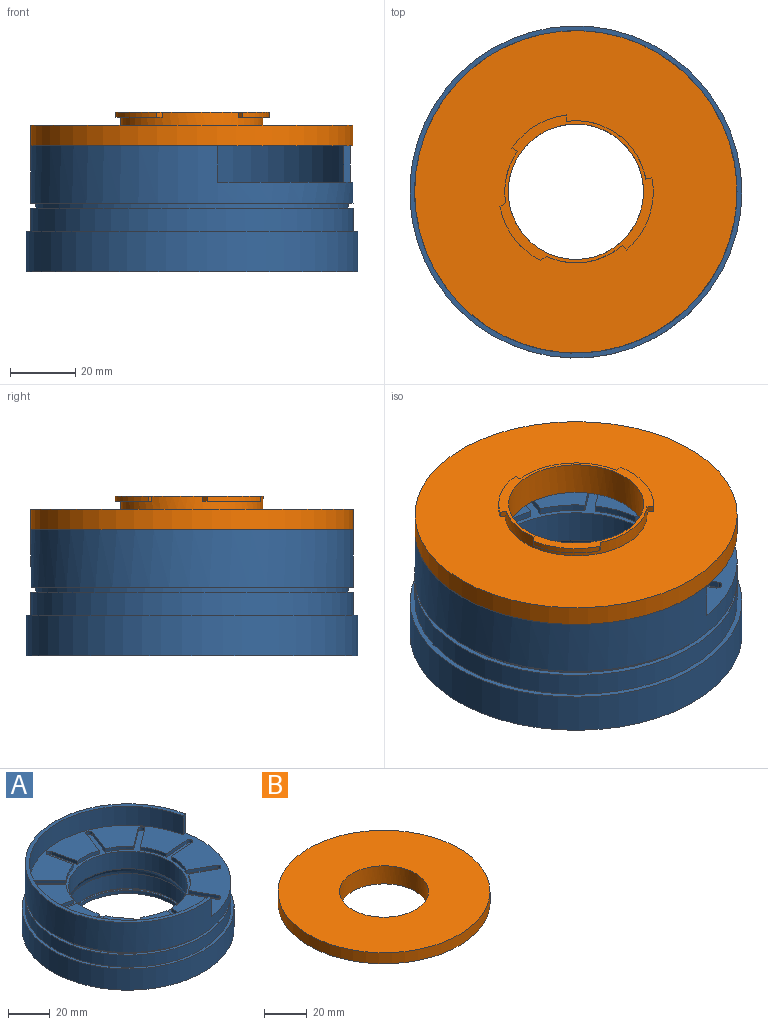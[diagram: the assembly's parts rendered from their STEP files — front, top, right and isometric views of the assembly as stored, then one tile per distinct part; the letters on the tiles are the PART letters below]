
ASSEMBLY  parts=2 mates=1
PART A: 65 faces, bbox 102.1x102.1x38.8 mm
  f0: cylinder r=49.57mm len=99.14mm, axis (0,0,-1), area 4618.4mm2, adj f2,f14,f22,f63,f64
  f1: cylinder r=47.57mm len=95.14mm, axis (0,0,-1), area 2494.3mm2, adj f2,f14,f63,f64
  f2: plane 97.14x96.49mm, normal (0,0,1), area 3856.3mm2, adj f0,f1,f3,f4,f5,f6,f7,f8
  f3: cylinder r=30mm len=9.74mm, axis (0,0,-1), area 27.8mm2, adj f2,f15,f32,f60
  f4: cylinder r=30mm len=13.45mm, axis (0,0,-1), area 27.8mm2, adj f2,f15,f57,f62
  f5: cylinder r=30mm len=12.9mm, axis (0,0,-1), area 27.8mm2, adj f2,f15,f54,f59
  f6: cylinder r=30mm len=11.01mm, axis (0,0,-1), area 27.8mm2, adj f2,f15,f51,f56
  f7: cylinder r=30mm len=13.73mm, axis (0,0,-1), area 27.8mm2, adj f2,f15,f48,f53
  f8: cylinder r=30mm len=12.08mm, axis (0,0,-1), area 27.8mm2, adj f2,f15,f45,f50
  f9: cylinder r=30mm len=12.07mm, axis (0,0,-1), area 27.8mm2, adj f2,f15,f42,f47
  f10: cylinder r=30mm len=13.73mm, axis (0,0,-1), area 27.8mm2, adj f2,f15,f39,f44
  f11: cylinder r=30mm len=11.02mm, axis (0,0,-1), area 27.8mm2, adj f2,f15,f36,f41
  f12: cylinder r=30mm len=12.89mm, axis (0,0,-1), area 27.8mm2, adj f2,f15,f33,f38
  f13: cylinder r=30mm len=13.45mm, axis (0,0,-1), area 27.8mm2, adj f2,f15,f30,f35
  f14: plane 99.14x98.22mm, normal (0,0,1), area 454.8mm2, adj f0,f1,f63,f64
  f15: plane 92x92mm, normal (0,0,1), area 842.9mm2, adj f3,f4,f5,f6,f7,f8,f9,f10
  f16: plane 102.14x102.14mm, normal (0,0,-1), area 5445.5mm2, adj f17,f29
  f17: cylinder r=51.07mm len=102.14mm, axis (0,0,1), area 4011mm2, adj f16,f18
  f18: plane 102.14x102.14mm, normal (0,0,1), area 474.2mm2, adj f17,f19
  f19: cylinder r=49.57mm len=99.14mm, axis (0,0,1), area 2216.5mm2, adj f18,f20
  f20: plane 99.14x99.14mm, normal (0,0,1), area 460.1mm2, adj f19,f21
  f21: cylinder r=48.07mm len=96.14mm, axis (0,0,1), area 453mm2, adj f20,f22
  f22: plane 99.14x99.14mm, normal (0,0,-1), area 460.1mm2, adj f0,f21
  f23: cylinder r=28.57mm len=57.15mm, axis (0,0,1), area 1838.8mm2, adj f15,f24
  f24: revolved ~59.15x59.15mm, area 686.4mm2, adj f23,f25
  f25: cylinder r=29.57mm len=59.15mm, axis (0,0,1), area 1635.3mm2, adj f24,f26
  f26: plane 61.15x61.15mm, normal (0,0,-1), area 189mm2, adj f25,f27
  f27: cylinder r=30.58mm len=61.15mm, axis (0,0,1), area 192.1mm2, adj f26,f28
  f28: plane 61.15x61.15mm, normal (0,0,1), area 189mm2, adj f27,f29
  f29: cylinder r=29.57mm len=59.15mm, axis (0,0,1), area 371.7mm2, adj f16,f28
  f30: plane 13.14x7.18mm, normal (0.88,0.48,0), area 29.9mm2, adj f2,f13,f15,f31
  f31: cylinder r=1.64mm len=3.08mm, axis (0,0,1), area 9.7mm2, adj f2,f15,f30,f32
  f32: plane 13.42x7.33mm, normal (-0.88,-0.48,0), area 30.6mm2, adj f2,f3,f15,f31
  f33: plane 14.94x2mm, normal (1,-0.07,0), area 29.9mm2, adj f2,f12,f15,f34
  f34: cylinder r=1.64mm len=3.22mm, axis (0,0,1), area 9.7mm2, adj f2,f15,f33,f35
  f35: plane 15.25x2mm, normal (-1,0.07,0), area 30.6mm2, adj f2,f13,f15,f34
  f36: plane 11.99x8.97mm, normal (0.8,-0.6,0), area 29.9mm2, adj f2,f11,f15,f37
  f37: cylinder r=1.64mm len=2.74mm, axis (0,0,1), area 9.7mm2, adj f2,f15,f36,f38
  f38: plane 12.24x9.16mm, normal (-0.8,0.6,0), area 30.6mm2, adj f2,f12,f15,f37
  f39: plane 14.03x5.23mm, normal (0.35,-0.94,0), area 29.9mm2, adj f2,f10,f15,f40
  f40: cylinder r=1.64mm len=3.18mm, axis (0,0,1), area 9.7mm2, adj f2,f15,f39,f41
  f41: plane 14.32x5.34mm, normal (-0.35,0.94,0), area 30.6mm2, adj f2,f11,f15,f40
  f42: plane 14.63x3.18mm, normal (-0.21,-0.98,0), area 29.9mm2, adj f2,f9,f15,f43
  f43: cylinder r=1.64mm len=3.15mm, axis (0,0,1), area 9.7mm2, adj f2,f15,f42,f44
  f44: plane 14.94x3.25mm, normal (0.21,0.98,0), area 30.6mm2, adj f2,f10,f15,f43
  f45: plane 10.59x10.59mm, normal (-0.71,-0.71,0), area 29.9mm2, adj f2,f8,f15,f46
  f46: cylinder r=1.64mm len=2.8mm, axis (0,0,1), area 9.7mm2, adj f2,f15,f45,f47
  f47: plane 10.81x10.81mm, normal (0.71,0.71,0), area 30.6mm2, adj f2,f9,f15,f46
  f48: plane 14.63x3.18mm, normal (-0.98,-0.21,0), area 29.9mm2, adj f2,f7,f15,f49
  f49: cylinder r=1.64mm len=3.24mm, axis (0,0,1), area 9.7mm2, adj f2,f15,f48,f50
  f50: plane 14.94x3.25mm, normal (0.98,0.21,0), area 30.6mm2, adj f2,f8,f15,f49
  f51: plane 14.03x5.23mm, normal (-0.94,0.35,0), area 29.9mm2, adj f2,f6,f15,f52
  f52: cylinder r=1.64mm len=3.04mm, axis (0,0,1), area 9.7mm2, adj f2,f15,f51,f53
  f53: plane 14.32x5.34mm, normal (0.94,-0.35,0), area 30.6mm2, adj f2,f7,f15,f52
  f54: plane 11.99x8.97mm, normal (-0.6,0.8,0), area 29.9mm2, adj f2,f5,f15,f55
  f55: cylinder r=1.64mm len=2.95mm, axis (0,0,1), area 9.7mm2, adj f2,f15,f54,f56
  f56: plane 12.24x9.16mm, normal (0.6,-0.8,0), area 30.6mm2, adj f2,f6,f15,f55
  f57: plane 14.94x2mm, normal (-0.07,1,0), area 29.9mm2, adj f2,f4,f15,f58
  f58: cylinder r=1.64mm len=3.26mm, axis (0,0,1), area 9.7mm2, adj f2,f15,f57,f59
  f59: plane 15.25x2mm, normal (0.07,-1,0), area 30.6mm2, adj f2,f5,f15,f58
  f60: plane 13.14x7.18mm, normal (0.48,0.88,0), area 29.9mm2, adj f2,f3,f15,f61
  f61: cylinder r=1.64mm len=2.9mm, axis (0,0,1), area 9.7mm2, adj f2,f15,f60,f62
  f62: plane 13.42x7.33mm, normal (-0.48,-0.88,0), area 30.6mm2, adj f2,f4,f15,f61
  f63: plane 11.2x1.96mm, normal (0.19,-0.98,0), area 22.4mm2, adj f0,f1,f2,f14
  f64: plane 11.2x1.97mm, normal (0.99,0.16,0), area 22.4mm2, adj f0,f1,f2,f14
PART B: 18 faces, bbox 99.1x99.1x10.4 mm
  f0: plane 17.87x14.23mm, normal (0,0,1), area 42mm2, adj f8,f9,f10,f12
  f1: plane 16.87x11.31mm, normal (0,0,1), area 37.8mm2, adj f2,f3,f4,f12
  f2: plane 1.65x1.61mm, normal (-0.56,0.83,0), area 3.2mm2, adj f1,f3,f12,f14
  f3: cylinder r=23.8mm len=16.87mm, axis (0,0,-1), area 33.5mm2, adj f1,f2,f4,f14
  f4: plane 1.96x1.65mm, normal (1,0,0), area 3.2mm2, adj f1,f3,f12,f14
  f5: plane 1.92x1.65mm, normal (-0.18,-0.98,0), area 3.2mm2, adj f6,f12,f13,f14
  f6: cylinder r=23.8mm len=22.16mm, axis (0,0,-1), area 40.5mm2, adj f5,f7,f13,f14
  f7: plane 1.65x1.47mm, normal (-0.75,0.66,0), area 3.2mm2, adj f6,f12,f13,f14
  f8: plane 1.75x1.65mm, normal (0.6,0.8,0), area 3.6mm2, adj f0,f9,f12,f14
  f9: cylinder r=23.8mm len=16.55mm, axis (0,0,-1), area 35.4mm2, adj f0,f8,f10,f14
  f10: plane 1.75x1.65mm, normal (-0.6,-0.8,0), area 3.6mm2, adj f0,f9,f12,f14
  f11: cylinder r=20.8mm len=41.6mm, axis (0,0,-1), area 1355.3mm2, adj f14,f15
  f12: cylinder r=21.85mm len=43.7mm, axis (0,0,-1), area 455.5mm2, adj f0,f1,f2,f4,f5,f7,f8,f10
  f13: plane 22.16x9.43mm, normal (0,0,1), area 45.9mm2, adj f5,f6,f7,f12
  f14: plane 47.15x45.49mm, normal (0,0,-1), area 266.4mm2, adj f2,f3,f4,f5,f6,f7,f8,f9
  f15: plane 99.14x99.14mm, normal (0,0,1), area 6360mm2, adj f11,f16
  f16: cylinder r=49.57mm len=99.14mm, axis (0,0,-1), area 1962.1mm2, adj f15,f17
  f17: plane 99.14x99.14mm, normal (0,0,-1), area 6219.3mm2, adj f12,f16
PLACE A at identity fixed
PLACE B rot(axis=(1,0,0),180deg) t=(0,0,23.57)mm
MATE planar B.f6 <-> A.f14  axis (0,0,-1) through (0,0,13.2)mm
